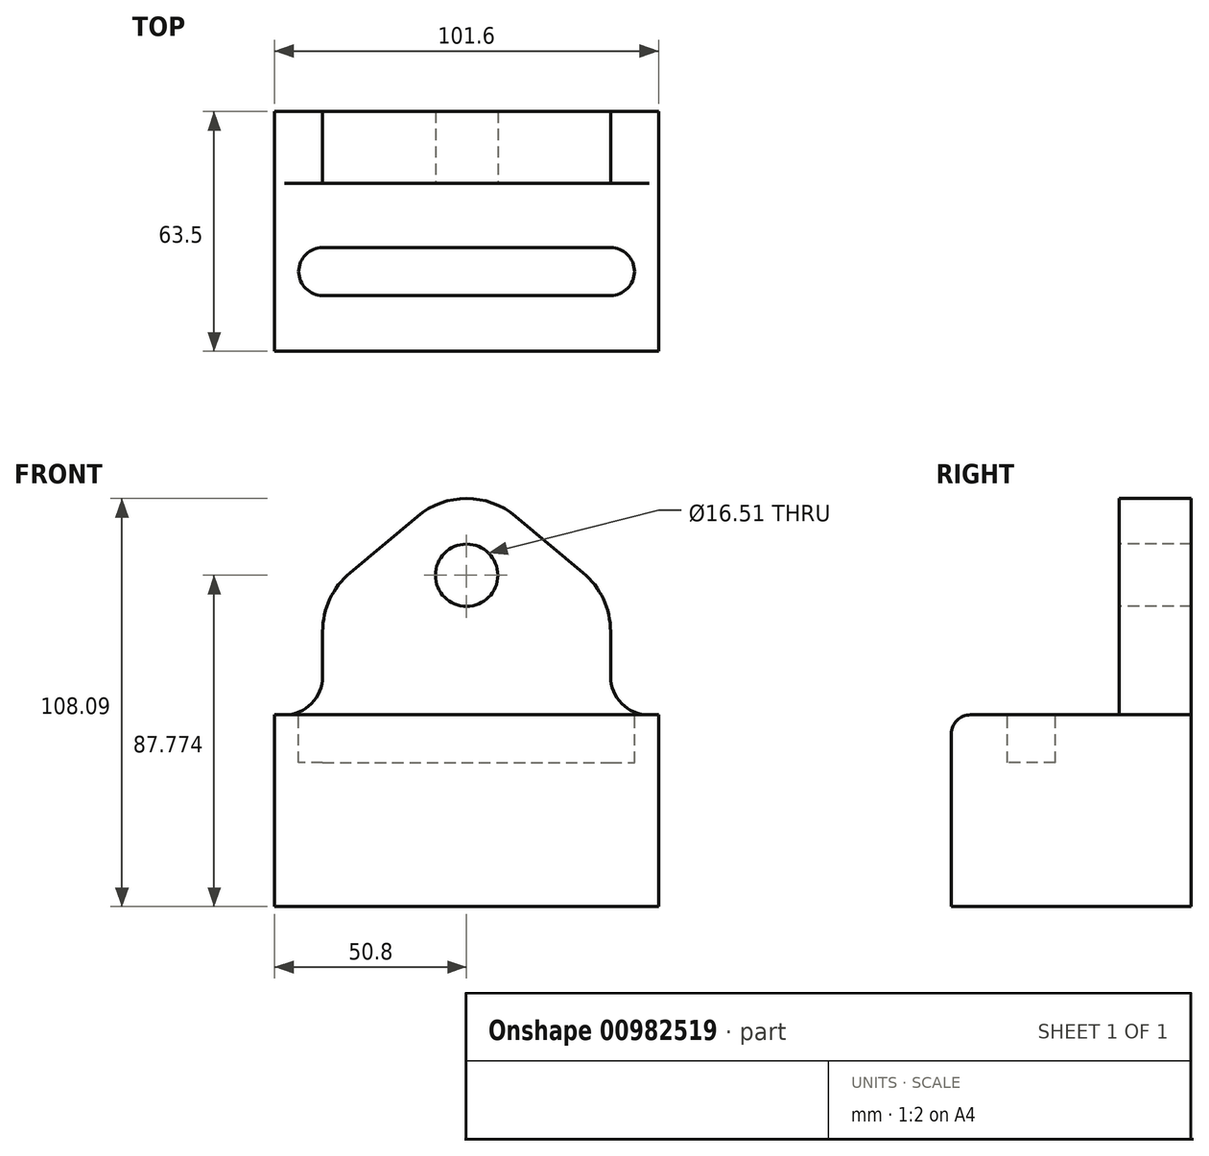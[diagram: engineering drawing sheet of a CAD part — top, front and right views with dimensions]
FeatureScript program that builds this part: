
annotation { "Feature Type Name" : "Feature", "Feature Type Description" : "" }
export const myFeature = defineFeature(function(context is Context, id is Id, definition is map)
    precondition{}
    {
        {
            var Q0;
            Q0=qCreatedBy(makeId("Top.planeOp"),FACE);
            var sketch = newSketch(context, id + "F0", { "sketchPlane" : qUnion([Q0])});
            skLineSegment(sketch, "E0.bottom", {"start": v(-50.8, 25.4) * mm, "end": v(50.8, 25.4) * mm});
            skLineSegment(sketch, "E0.top", {"start": v(-50.8, -38.1) * mm, "end": v(50.8, -38.1) * mm});
            skLineSegment(sketch, "E0.left", {"start": v(-50.8, 25.4) * mm, "end": v(-50.8, -38.1) * mm});
            skLineSegment(sketch, "E0.right", {"start": v(50.8, 25.4) * mm, "end": v(50.8, -38.1) * mm});
            skSolve(sketch);
        }
        {
            var Q0;
            Q0 = qSketchRegion(id + "F0", true);
            extrude(context, id + "F1", {"entities" : qUnion([Q0]), "depth" : 50.8 * mm, "offsetDistance" : 25.4 * mm});
        }
        {
            var Q0;
            Q0=makeQuery(id+"F1.opExtrude","CAP_EDGE",EDGE,{"disambiguationData":[OSD([sQuery(id+"F0.wireOp",EDGE,"E0.top")])],"isStart":false});
            fillet(context, id + "F2", {"entities" : qUnion([Q0]), "radius" : 5.08 * mm, "tangentPropagation" : true, "allowEdgeOverflow" : false});
        }
        {
            var Q0;
            Q0=makeQuery(id+"F1.opExtrude","CAP_FACE",FACE,{"disambiguationData":[OSD([sQuery(id+"F0.wireOp",EDGE,"E0.bottom"),sQuery(id+"F0.wireOp",EDGE,"E0.top"),sQuery(id+"F0.wireOp",EDGE,"E0.left"),sQuery(id+"F0.wireOp",EDGE,"E0.right")])],"isStart":false});
            var sketch = newSketch(context, id + "F3", { "sketchPlane" : qUnion([Q0])});
            skLineSegment(sketch, "E1.bottom", {"start": v(-38.1, -10.63) * mm, "end": v(38.1, -10.63) * mm});
            skLineSegment(sketch, "E1.top", {"start": v(-38.1, -23.33) * mm, "end": v(38.1, -23.33) * mm});
            skArc(sketch, "E2", {"start": v(-38.1, -10.63) * mm, "mid": v(-44.45, -16.98) * mm, "end": v(-38.1, -23.33) * mm});
            skArc(sketch, "E3", {"start": v(38.1, -23.33) * mm, "mid": v(44.45, -16.98) * mm, "end": v(38.1, -10.63) * mm});
            skSolve(sketch);
        }
        {
            var Q0;
            Q0 = qSketchRegion(id + "F3", true);
            extrude(context, id + "F4", {"entities" : qUnion([Q0]), "operationType" : NewBodyOperationType.REMOVE, "oppositeDirection" : true, "depth" : 12.7 * mm, "offsetDistance" : 25.4 * mm});
        }
        {
            var Q0;
            Q0=makeQuery(id+"F1.opExtrude","CAP_FACE",FACE,{"disambiguationData":[OSD([sQuery(id+"F0.wireOp",EDGE,"E0.bottom"),sQuery(id+"F0.wireOp",EDGE,"E0.top"),sQuery(id+"F0.wireOp",EDGE,"E0.left"),sQuery(id+"F0.wireOp",EDGE,"E0.right")])],"isStart":false});
            var sketch = newSketch(context, id + "F5", { "sketchPlane" : qUnion([Q0])});
            skLineSegment(sketch, "E4.bottom", {"start": v(-50.8, 25.4) * mm, "end": v(50.8, 25.4) * mm});
            skLineSegment(sketch, "E4.top", {"start": v(-50.8, 6.35) * mm, "end": v(50.8, 6.35) * mm});
            skLineSegment(sketch, "E4.left", {"start": v(-50.8, 25.4) * mm, "end": v(-50.8, 6.35) * mm});
            skLineSegment(sketch, "E4.right", {"start": v(50.8, 25.4) * mm, "end": v(50.8, 6.35) * mm});
            skSolve(sketch);
        }
        {
            var Q0;
            Q0 = qSketchRegion(id + "F5", true);
            extrude(context, id + "F6", {"entities" : qUnion([Q0]), "operationType" : NewBodyOperationType.ADD, "depth" : 63.5 * mm, "offsetDistance" : 25.4 * mm});
        }
        {
            var Q0;
            Q0=makeQuery(id+"F6.opExtrude","SWEPT_FACE",FACE,{"disambiguationData":[OSD([sQuery(id+"F5.wireOp",EDGE,"E4.top")])]});
            var sketch = newSketch(context, id + "F7", { "sketchPlane" : qUnion([Q0])});
            skLineSegment(sketch, "E5", {"start": v(50.8, 50.8) * mm, "end": v(38.1, 50.8) * mm});
            skLineSegment(sketch, "E6", {"start": v(38.1, 50.8) * mm, "end": v(38.1, 82.33) * mm});
            skLineSegment(sketch, "E7", {"start": v(38.1, 82.33) * mm, "end": v(0, 114.3) * mm});
            skLineSegment(sketch, "E8", {"start": v(0, 114.3) * mm, "end": v(-38.1, 82.33) * mm});
            skLineSegment(sketch, "E9", {"start": v(-38.1, 82.33) * mm, "end": v(-38.1, 50.8) * mm});
            skLineSegment(sketch, "E10", {"start": v(-38.1, 50.8) * mm, "end": v(-50.8, 50.8) * mm});
            skSolve(sketch);
        }
        {
            var Q0;
            Q0 = qSketchRegion(id + "F7", true);
            var Q1;
            {var subQ2=sQuery(id+"F7.wireOp",EDGE,"E8");Q1=makeQuery(id+"F7.imprint","IMPRINT",FACE,{"disambiguationData":[TD([[makeQuery(id+"F7.imprint","IMPRINT",EDGE,{"derivedFrom":subQ2}),-1.0]])]});}
            var Q2;
            Q2=makeQuery(id+"F7.imprint","IMPRINT",FACE,{"disambiguationData":[TD([[makeQuery(id+"F7.imprint","IMPRINT",EDGE,{"derivedFrom":sQuery(id+"F7.wireOp",EDGE,"E5")}),1.0]])]});
            extrude(context, id + "F8", {"entities" : qUnion([Q0, Q1, Q2]), "operationType" : NewBodyOperationType.REMOVE, "oppositeDirection" : true, "depth" : 25.4 * mm, "offsetDistance" : 25.4 * mm});
        }
        {
            var Q0;
            Q0=makeQuery(id+"F8.boolean.opBoolean","COPY",EDGE,{"derivedFrom":makeQuery(id+"F8.opExtrude","SWEPT_EDGE",EDGE,{"disambiguationData":[OSD([sQuery(id+"F7.wireOp",EDGE,"E6"),sQuery(id+"F7.wireOp",EDGE,"E7")])]})});
            var Q1;
            Q1=makeQuery(id+"F8.boolean.opBoolean","COPY",EDGE,{"derivedFrom":makeQuery(id+"F8.opExtrude","SWEPT_EDGE",EDGE,{"disambiguationData":[OSD([sQuery(id+"F7.wireOp",EDGE,"E8"),sQuery(id+"F7.wireOp",EDGE,"E9")])]})});
            var Q2;
            {var subQ0=sQuery(id+"F7.wireOp",EDGE,"E8");var subQ1=sQuery(id+"F7.wireOp",EDGE,"E7");var subQ2=sQuery(id+"F5.wireOp",EDGE,"E4.top");Q2=makeQuery(id+"F8.boolean.opBoolean","MERGE",EDGE,{"derivedFrom":[],"fromTools":[makeQuery(id+"F8.opExtrude","SWEPT_EDGE",EDGE,{"disambiguationData":[OSD([subQ2,subQ1,subQ0]),OD(0.0)]}),makeQuery(id+"F8.opExtrude","SWEPT_EDGE",EDGE,{"disambiguationData":[OSD([subQ2,subQ1,subQ0]),OD(1.0)]})]});}
            fillet(context, id + "F9", {"entities" : qUnion([Q0, Q1, Q2]), "radius" : 20.32 * mm, "tangentPropagation" : true, "allowEdgeOverflow" : false});
        }
        {
            var Q0;
            Q0=makeQuery(id+"F8.boolean.opBoolean","COPY",EDGE,{"derivedFrom":makeQuery(id+"F8.opExtrude","SWEPT_EDGE",EDGE,{"disambiguationData":[OSD([sQuery(id+"F5.wireOp",EDGE,"E4.top"),sQuery(id+"F7.wireOp",EDGE,"E5"),sQuery(id+"F7.wireOp",EDGE,"E6")])]})});
            var Q1;
            Q1=makeQuery(id+"F8.boolean.opBoolean","COPY",EDGE,{"derivedFrom":makeQuery(id+"F8.opExtrude","SWEPT_EDGE",EDGE,{"disambiguationData":[OSD([sQuery(id+"F5.wireOp",EDGE,"E4.top"),sQuery(id+"F7.wireOp",EDGE,"E9"),sQuery(id+"F7.wireOp",EDGE,"E10")])]})});
            fillet(context, id + "F10", {"entities" : qUnion([Q0, Q1]), "radius" : 10.16 * mm, "tangentPropagation" : true, "allowEdgeOverflow" : false});
        }
        {
            var Q0;
            Q0=makeQuery(id+"F6.opExtrude","SWEPT_FACE",FACE,{"disambiguationData":[OSD([sQuery(id+"F5.wireOp",EDGE,"E4.top")])]});
            var sketch = newSketch(context, id + "F11", { "sketchPlane" : qUnion([Q0])});
            skCircle(sketch, "E11", {"center": v(0, 87.77) * mm, "radius": 8.26 * mm});
            skSolve(sketch);
        }
        {
            var Q0;
            Q0 = qSketchRegion(id + "F11", true);
            extrude(context, id + "F12", {"entities" : qUnion([Q0]), "operationType" : NewBodyOperationType.REMOVE, "oppositeDirection" : true, "depth" : 25.4 * mm, "offsetDistance" : 25.4 * mm});
        }
    });
